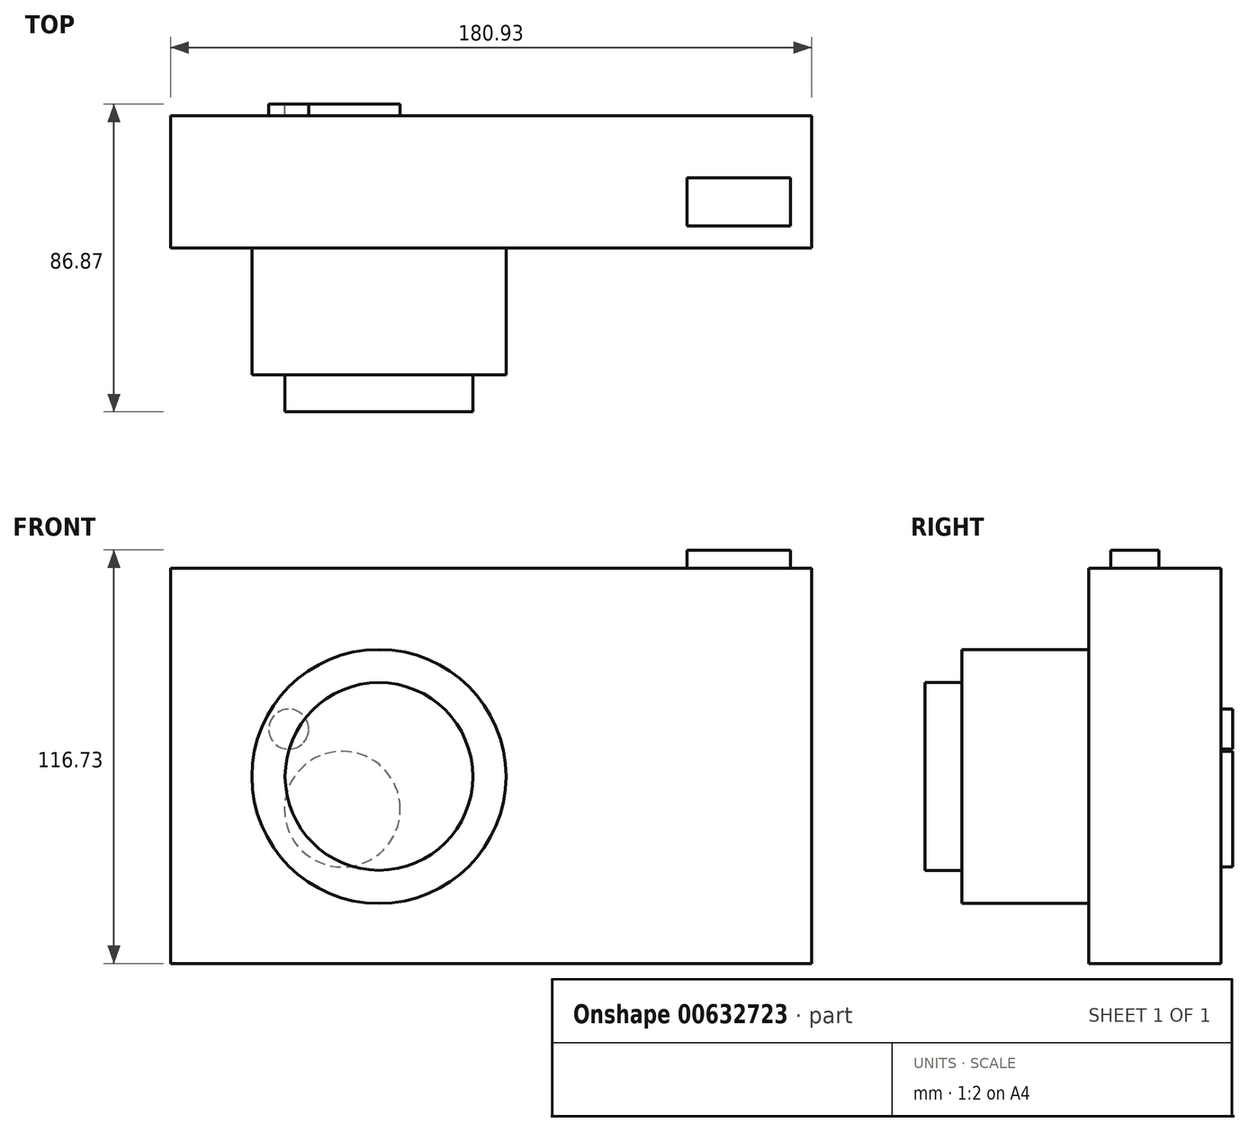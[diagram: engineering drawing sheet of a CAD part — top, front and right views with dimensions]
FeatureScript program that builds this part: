
annotation { "Feature Type Name" : "Feature", "Feature Type Description" : "" }
export const myFeature = defineFeature(function(context is Context, id is Id, definition is map)
    precondition{}
    {
        {
            var Q0;
            Q0=qCreatedBy(makeId("Front.planeOp"),FACE);
            var sketch = newSketch(context, id + "F0", { "sketchPlane" : qUnion([Q0])});
            skLineSegment(sketch, "E0.bottom", {"start": v(-116.05, 40.84) * mm, "end": v(64.88, 40.84) * mm});
            skLineSegment(sketch, "E0.top", {"start": v(-116.05, -70.8) * mm, "end": v(64.88, -70.8) * mm});
            skLineSegment(sketch, "E0.left", {"start": v(-116.05, 40.84) * mm, "end": v(-116.05, -70.8) * mm});
            skLineSegment(sketch, "E0.right", {"start": v(64.88, 40.84) * mm, "end": v(64.88, -70.8) * mm});
            skSolve(sketch);
        }
        {
            var Q0;
            Q0=makeQuery(id+"F0.imprint","IMPRINT",FACE,{"disambiguationData":[TD([[makeQuery(id+"F0.imprint","IMPRINT",EDGE,{"derivedFrom":sQuery(id+"F0.wireOp",EDGE,"E0.bottom")}),-1.0]])]});
            extrude(context, id + "F1", {"entities" : qUnion([Q0]), "depth" : 25.4 * mm, "offsetDistance" : 25.4 * mm});
        }
        {
            var Q0;
            Q0=makeQuery(id+"F1.opExtrude","CAP_FACE",FACE,{"disambiguationData":[OSD([sQuery(id+"F0.wireOp",EDGE,"E0.bottom"),sQuery(id+"F0.wireOp",EDGE,"E0.top"),sQuery(id+"F0.wireOp",EDGE,"E0.left"),sQuery(id+"F0.wireOp",EDGE,"E0.right")])],"isStart":false});
            var sketch = newSketch(context, id + "F2", { "sketchPlane" : qUnion([Q0])});
            skCircle(sketch, "E1", {"center": v(-57.25, -18.02) * mm, "radius": 35.86 * mm});
            skSolve(sketch);
        }
        {
            var Q0;
            Q0=makeQuery(id+"F2.imprint","IMPRINT",FACE,{"disambiguationData":[TD([[makeQuery(id+"F2.imprint","IMPRINT",EDGE,{"derivedFrom":sQuery(id+"F2.wireOp",EDGE,"E1")}),1.0]])]});
            extrude(context, id + "F3", {"entities" : qUnion([Q0]), "operationType" : NewBodyOperationType.ADD, "depth" : 35.81 * mm, "offsetDistance" : 25.4 * mm});
        }
        {
            var Q0;
            Q0=makeQuery(id+"F3.opExtrude","CAP_FACE",FACE,{"disambiguationData":[OSD([sQuery(id+"F2.wireOp",EDGE,"E1")])],"isStart":false});
            var sketch = newSketch(context, id + "F4", { "sketchPlane" : qUnion([Q0])});
            skCircle(sketch, "E2", {"center": v(-57.25, -18.02) * mm, "radius": 26.5 * mm});
            skSolve(sketch);
        }
        {
            var Q0;
            Q0=makeQuery(id+"F4.imprint","IMPRINT",FACE,{"disambiguationData":[TD([[makeQuery(id+"F4.imprint","IMPRINT",EDGE,{"derivedFrom":sQuery(id+"F4.wireOp",EDGE,"E2")}),1.0]])]});
            extrude(context, id + "F5", {"entities" : qUnion([Q0]), "operationType" : NewBodyOperationType.ADD, "depth" : 10.4 * mm, "offsetDistance" : 25.4 * mm});
        }
        {
            var Q0;
            Q0=makeQuery(id+"F1.opExtrude","SWEPT_FACE",FACE,{"disambiguationData":[OSD([sQuery(id+"F0.wireOp",EDGE,"E0.bottom")])]});
            var sketch = newSketch(context, id + "F6", { "sketchPlane" : qUnion([Q0])});
            skLineSegment(sketch, "E3.bottom", {"start": v(29.78, -5.5) * mm, "end": v(58.94, -5.5) * mm});
            skLineSegment(sketch, "E3.top", {"start": v(29.78, -19.1) * mm, "end": v(58.94, -19.1) * mm});
            skLineSegment(sketch, "E3.left", {"start": v(29.78, -5.5) * mm, "end": v(29.78, -19.1) * mm});
            skLineSegment(sketch, "E3.right", {"start": v(58.94, -5.5) * mm, "end": v(58.94, -19.1) * mm});
            skSolve(sketch);
        }
        {
            var Q0;
            Q0=makeQuery(id+"F6.imprint","IMPRINT",FACE,{"disambiguationData":[TD([[makeQuery(id+"F6.imprint","IMPRINT",EDGE,{"derivedFrom":sQuery(id+"F6.wireOp",EDGE,"E3.bottom")}),-1.0]])]});
            extrude(context, id + "F7", {"entities" : qUnion([Q0]), "operationType" : NewBodyOperationType.ADD, "depth" : 5.08 * mm, "offsetDistance" : 25.4 * mm});
        }
        {
            var Q0;
            Q0=makeQuery(id+"F1.opExtrude","CAP_FACE",FACE,{"disambiguationData":[OSD([sQuery(id+"F0.wireOp",EDGE,"E0.bottom"),sQuery(id+"F0.wireOp",EDGE,"E0.top"),sQuery(id+"F0.wireOp",EDGE,"E0.left"),sQuery(id+"F0.wireOp",EDGE,"E0.right")])],"isStart":true});
            extrude(context, id + "F8", {"entities" : qUnion([Q0]), "operationType" : NewBodyOperationType.ADD, "depth" : 11.94 * mm, "offsetDistance" : 25.4 * mm});
        }
        {
            var Q0;
            Q0=makeQuery(id+"F8.opExtrude","CAP_FACE",FACE,{"disambiguationData":[OSD([sQuery(id+"F0.wireOp",EDGE,"E0.bottom"),sQuery(id+"F0.wireOp",EDGE,"E0.top"),sQuery(id+"F0.wireOp",EDGE,"E0.left"),sQuery(id+"F0.wireOp",EDGE,"E0.right")])],"isStart":false});
            var sketch = newSketch(context, id + "F9", { "sketchPlane" : qUnion([Q0])});
            skLineSegment(sketch, "E4.bottom", {"start": v(-59.84, 31.97) * mm, "end": v(-24.64, 31.97) * mm});
            skLineSegment(sketch, "E4.top", {"start": v(-59.84, 19.3) * mm, "end": v(-24.64, 19.3) * mm});
            skLineSegment(sketch, "E4.left", {"start": v(-59.84, 31.97) * mm, "end": v(-59.84, 19.3) * mm});
            skLineSegment(sketch, "E4.right", {"start": v(-24.64, 31.97) * mm, "end": v(-24.64, 19.3) * mm});
            skSolve(sketch);
        }
        {
            var Q0;
            Q0=makeQuery(id+"F9.imprint","IMPRINT",FACE,{"disambiguationData":[TD([[makeQuery(id+"F9.imprint","IMPRINT",EDGE,{"derivedFrom":sQuery(id+"F9.wireOp",EDGE,"E4.bottom")}),1.0]])]});
            var sketch = newSketch(context, id + "F10", { "sketchPlane" : qUnion([Q0])});
            skCircle(sketch, "E5", {"center": v(67.6, -27.26) * mm, "radius": 16.35 * mm});
            skCircle(sketch, "E6", {"center": v(46.25, -3.42) * mm, "radius": 5.12 * mm});
            skCircle(sketch, "E7", {"center": v(82.73, -4.66) * mm, "radius": 5.64 * mm});
            skSolve(sketch);
        }
        {
            var Q0;
            Q0=makeQuery(id+"F10.imprint","IMPRINT",FACE,{"disambiguationData":[TD([[makeQuery(id+"F10.imprint","IMPRINT",EDGE,{"derivedFrom":sQuery(id+"F10.wireOp",EDGE,"E5")}),1.0]])]});
            var Q1;
            Q1=makeQuery(id+"F10.imprint","IMPRINT",FACE,{"disambiguationData":[TD([[makeQuery(id+"F10.imprint","IMPRINT",EDGE,{"derivedFrom":sQuery(id+"F10.wireOp",EDGE,"E7")}),1.0]])]});
            extrude(context, id + "F11", {"entities" : qUnion([Q0, Q1]), "operationType" : NewBodyOperationType.ADD, "depth" : 3.3 * mm, "offsetDistance" : 25.4 * mm});
        }
    });
